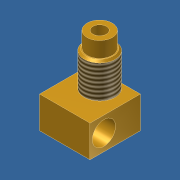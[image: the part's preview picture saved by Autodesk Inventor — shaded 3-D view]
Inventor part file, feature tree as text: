
AUTODESK INVENTOR PART (.ipt)
format: ipt  version: unknown  size: 225,792 bytes
history: native  units: mm
features: sketch x4, hole x2, revolve x1, plane x1, extrude x1, thread x1, chamfer x1, projected_geometry x1
ambient origin geometry x8: Origin, YZ Plane, XZ Plane, XY Plane, X Axis, Y Axis, Z Axis, Center Point
feature tree (12):
  revolve  "Revolution1"  [1 undecoded]
  plane  "Work Plane1"
  extrude  "Extrusion1"  Depth=4.0mm
  hole  "Hole1"  [1 undecoded]
  hole  "Hole2"  [1 undecoded]
  thread  "Thread2"  [1 undecoded]
  chamfer  "Chamfer2"  Distance=8.2mm
  sketch  "Sketch2"  dims[d0=0.2mm d6=24.2mm]
  sketch  "Sketch3"  dims[d7=4.0mm d11=4.0mm]
  sketch  "Sketch4"  dims[d12=90.0deg d13=90.0deg]
  sketch  "Sketch5"  dims[d15=13.0mm d16=13.0mm d17=4.0mm d18=8.2mm d19=0.0mm d20=3.6mm d21=4.0mm d22=6.0mm d23=6.0mm d24=4.0mm d25=2.0mm d26=90.0deg d27=8.0mm d28=20.594885mm d34=1.75mm d36=14.0mm d37=10.995574mm d38=8.726646mm d39=2.2mm d40=4.0mm d41=1.5mm d42=6.0mm d43=4.0mm d44=2.0mm d45=90.0deg d46=5.0mm d47=20.594885mm d48=0.6mm d50=-3.0mm d51=0.5mm d52=10.0mm d53=0.0mm d54=0.5mm d55=2.0mm d56=45.0deg d57=3.2385mm]
  projected_geometry  "Project Cut Edges1"
note: 4 required parameter values undecoded (feature->parameter linkage not recoverable at this tier; creation-order binding heuristic only, values carry confidence <= 0.55)